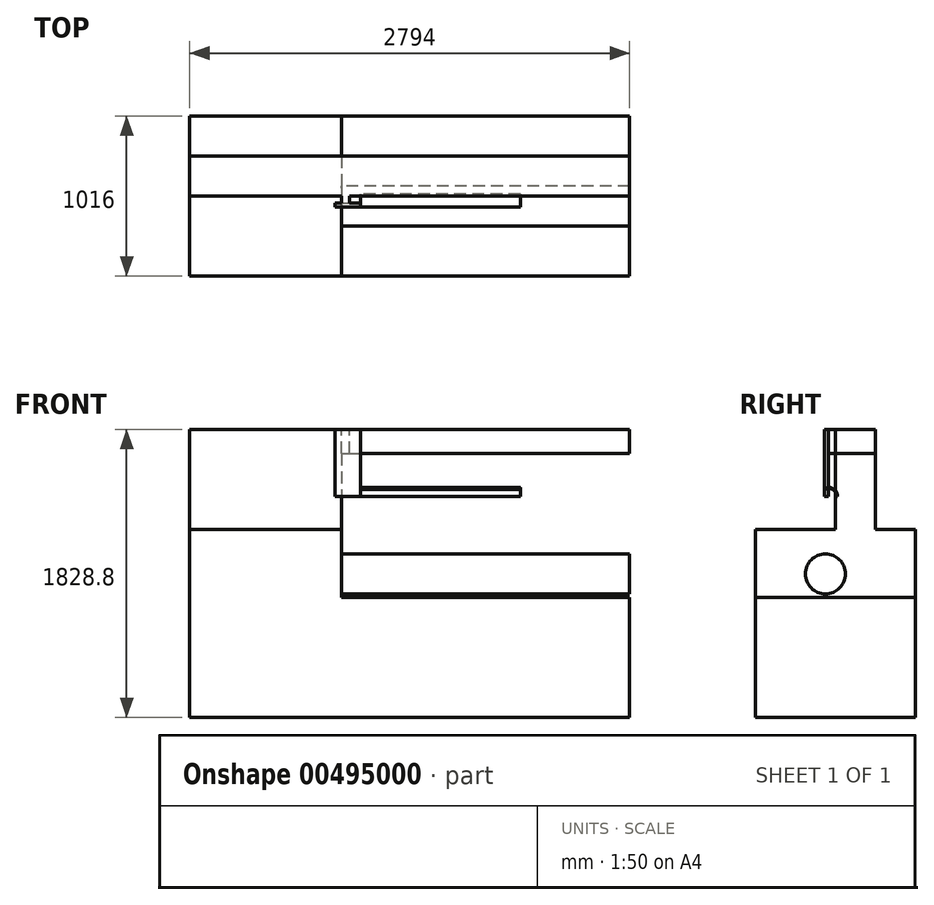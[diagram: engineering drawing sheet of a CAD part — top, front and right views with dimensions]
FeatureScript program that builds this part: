
annotation { "Feature Type Name" : "Feature", "Feature Type Description" : "" }
export const myFeature = defineFeature(function(context is Context, id is Id, definition is map)
    precondition{}
    {
        {
            var Q0;
            Q0=qCreatedBy(makeId("Front.planeOp"),FACE);
            var sketch = newSketch(context, id + "F0", { "sketchPlane" : qUnion([Q0])});
            skLineSegment(sketch, "E0.bottom", {"start": v(0, 0) * mm, "end": v(2794, 0) * mm});
            skLineSegment(sketch, "E0.top", {"start": v(0, 1828.8) * mm, "end": v(2794, 1828.8) * mm});
            skLineSegment(sketch, "E0.left", {"start": v(0, 0) * mm, "end": v(0, 1828.8) * mm});
            skLineSegment(sketch, "E0.right", {"start": v(2794, 0) * mm, "end": v(2794, 1828.8) * mm});
            skSolve(sketch);
        }
        {
            var Q0;
            Q0=makeQuery(id+"F0.imprint","IMPRINT",FACE,{"disambiguationData":[TD([[makeQuery(id+"F0.imprint","IMPRINT",EDGE,{"derivedFrom":sQuery(id+"F0.wireOp",EDGE,"E0.bottom")}),1.0]])]});
            extrude(context, id + "F1", {"entities" : qUnion([Q0]), "oppositeDirection" : true, "depth" : 1016 * mm});
        }
        {
            var Q0;
            Q0=makeQuery(id+"F1.opExtrude","CAP_FACE",FACE,{"disambiguationData":[OSD([sQuery(id+"F0.wireOp",EDGE,"E0.bottom"),sQuery(id+"F0.wireOp",EDGE,"E0.top"),sQuery(id+"F0.wireOp",EDGE,"E0.left"),sQuery(id+"F0.wireOp",EDGE,"E0.right")])],"isStart":true});
            var sketch = newSketch(context, id + "F2", { "sketchPlane" : qUnion([Q0])});
            skLineSegment(sketch, "E1.bottom", {"start": v(2794, 762) * mm, "end": v(965.2, 762) * mm});
            skLineSegment(sketch, "E1.top", {"start": v(2794, 1676.4) * mm, "end": v(965.2, 1676.4) * mm});
            skLineSegment(sketch, "E1.left", {"start": v(2794, 762) * mm, "end": v(2794, 1676.4) * mm});
            skLineSegment(sketch, "E1.right", {"start": v(965.2, 762) * mm, "end": v(965.2, 1676.4) * mm});
            skSolve(sketch);
        }
        {
            var Q0;
            Q0=makeQuery(id+"F2.imprint","IMPRINT",FACE,{"disambiguationData":[TD([[makeQuery(id+"F2.imprint","IMPRINT",EDGE,{"derivedFrom":sQuery(id+"F2.wireOp",EDGE,"E1.bottom")}),-1.0]])]});
            extrude(context, id + "F3", {"entities" : qUnion([Q0]), "operationType" : NewBodyOperationType.REMOVE, "endBound" : BoundingType.THROUGH_ALL, "oppositeDirection" : true, "depth" : 1016 * mm});
        }
        {
            var Q0;
            Q0=makeQuery(id+"F1.opExtrude","SWEPT_FACE",FACE,{"disambiguationData":[OSD([sQuery(id+"F0.wireOp",EDGE,"E0.top")])]});
            var sketch = newSketch(context, id + "F4", { "sketchPlane" : qUnion([Q0])});
            skLineSegment(sketch, "E2.bottom", {"start": v(0, 0) * mm, "end": v(2794, 0) * mm});
            skLineSegment(sketch, "E2.top", {"start": v(0, 508) * mm, "end": v(2794, 508) * mm});
            skLineSegment(sketch, "E2.left", {"start": v(0, 0) * mm, "end": v(0, 508) * mm});
            skLineSegment(sketch, "E2.right", {"start": v(2794, 0) * mm, "end": v(2794, 508) * mm});
            skSolve(sketch);
        }
        {
            var Q0;
            Q0=makeQuery(id+"F4.imprint","IMPRINT",FACE,{"disambiguationData":[TD([[makeQuery(id+"F4.imprint","IMPRINT",EDGE,{"derivedFrom":sQuery(id+"F4.wireOp",EDGE,"E2.bottom")}),1.0]])]});
            extrude(context, id + "F5", {"entities" : qUnion([Q0]), "operationType" : NewBodyOperationType.REMOVE, "oppositeDirection" : true, "depth" : 635 * mm});
        }
        {
            var Q0;
            Q0=makeQuery(id+"F1.opExtrude","SWEPT_FACE",FACE,{"disambiguationData":[OSD([sQuery(id+"F0.wireOp",EDGE,"E0.top")])]});
            var sketch = newSketch(context, id + "F6", { "sketchPlane" : qUnion([Q0])});
            skLineSegment(sketch, "E3.bottom", {"start": v(0, 1016) * mm, "end": v(2794, 1016) * mm});
            skLineSegment(sketch, "E3.top", {"start": v(0, 762) * mm, "end": v(2794, 762) * mm});
            skLineSegment(sketch, "E3.left", {"start": v(0, 1016) * mm, "end": v(0, 762) * mm});
            skLineSegment(sketch, "E3.right", {"start": v(2794, 1016) * mm, "end": v(2794, 762) * mm});
            skSolve(sketch);
        }
        {
            var Q0;
            Q0=makeQuery(id+"F6.imprint","IMPRINT",FACE,{"disambiguationData":[TD([[makeQuery(id+"F6.imprint","IMPRINT",EDGE,{"derivedFrom":sQuery(id+"F6.wireOp",EDGE,"E3.bottom")}),-1.0]])]});
            extrude(context, id + "F7", {"entities" : qUnion([Q0]), "operationType" : NewBodyOperationType.REMOVE, "oppositeDirection" : true, "depth" : 635 * mm});
        }
        {
            var Q0;
            Q0=makeQuery(id+"F3.boolean.opBoolean","COPY",FACE,{"derivedFrom":makeQuery(id+"F3.opExtrude","SWEPT_FACE",FACE,{"disambiguationData":[OSD([sQuery(id+"F2.wireOp",EDGE,"E1.right")])]})});
            var sketch = newSketch(context, id + "F8", { "sketchPlane" : qUnion([Q0])});
            skCircle(sketch, "E4", {"center": v(442.96, 911.98) * mm, "radius": 127 * mm});
            skSolve(sketch);
        }
        {
            var Q0;
            Q0 = qSketchRegion(id + "F8", true);
            extrude(context, id + "F9", {"entities" : qUnion([Q0]), "operationType" : NewBodyOperationType.ADD, "depth" : 1828.8 * mm});
        }
        {
            var Q0;
            Q0=makeQuery(id+"F5.boolean.opBoolean","COPY",FACE,{"derivedFrom":makeQuery(id+"F5.opExtrude","SWEPT_FACE",FACE,{"disambiguationData":[OSD([sQuery(id+"F4.wireOp",EDGE,"E2.top")])]})});
            var sketch = newSketch(context, id + "F10", { "sketchPlane" : qUnion([Q0])});
            skLineSegment(sketch, "E5.bottom", {"start": v(965.2, 1676.4) * mm, "end": v(1016, 1676.4) * mm});
            skLineSegment(sketch, "E5.top", {"start": v(965.2, 1828.8) * mm, "end": v(1016, 1828.8) * mm});
            skLineSegment(sketch, "E5.left", {"start": v(965.2, 1676.4) * mm, "end": v(965.2, 1828.8) * mm});
            skLineSegment(sketch, "E5.right", {"start": v(1016, 1676.4) * mm, "end": v(1016, 1828.8) * mm});
            skSolve(sketch);
        }
        {
            var Q0;
            Q0=makeQuery(id+"F10.imprint","IMPRINT",FACE,{"disambiguationData":[TD([[makeQuery(id+"F10.imprint","IMPRINT",EDGE,{"derivedFrom":sQuery(id+"F10.wireOp",EDGE,"E5.bottom")}),1.0]])]});
            extrude(context, id + "F11", {"entities" : qUnion([Q0]), "operationType" : NewBodyOperationType.ADD, "depth" : 44.45 * mm});
        }
        {
            var Q0;
            Q0=makeQuery(id+"F11.opExtrude","CAP_FACE",FACE,{"disambiguationData":[OSD([sQuery(id+"F10.wireOp",EDGE,"E5.bottom"),sQuery(id+"F10.wireOp",EDGE,"E5.top"),sQuery(id+"F10.wireOp",EDGE,"E5.left"),sQuery(id+"F10.wireOp",EDGE,"E5.right")])],"isStart":false});
            var sketch = newSketch(context, id + "F12", { "sketchPlane" : qUnion([Q0])});
            skLineSegment(sketch, "E6.bottom", {"start": v(1083.52, 1828.8) * mm, "end": v(922.15, 1828.8) * mm});
            skLineSegment(sketch, "E6.top", {"start": v(1083.52, 1403.65) * mm, "end": v(922.15, 1403.65) * mm});
            skLineSegment(sketch, "E6.left", {"start": v(1083.52, 1828.8) * mm, "end": v(1083.52, 1403.65) * mm});
            skLineSegment(sketch, "E6.right", {"start": v(922.15, 1828.8) * mm, "end": v(922.15, 1403.65) * mm});
            skSolve(sketch);
        }
        {
            var Q0;
            Q0 = qSketchRegion(id + "F12", true);
            extrude(context, id + "F13", {"entities" : qUnion([Q0]), "operationType" : NewBodyOperationType.ADD, "depth" : 25.4 * mm});
        }
        {
            var Q0;
            Q0=makeQuery(id+"F13.opExtrude","SWEPT_FACE",FACE,{"disambiguationData":[OSD([sQuery(id+"F12.wireOp",EDGE,"E6.left")])]});
            var sketch = newSketch(context, id + "F14", { "sketchPlane" : qUnion([Q0])});
            skArc(sketch, "E7", {"start": v(520.57, 1403.65) * mm, "mid": v(493.57, 1452.13) * mm, "end": v(438.15, 1454.7) * mm});
            skArc(sketch, "E8.0", {"start": v(514.22, 1403.65) * mm, "mid": v(490.23, 1446.73) * mm, "end": v(440.98, 1449.02) * mm});
            skLineSegment(sketch, "E9", {"start": v(440.98, 1449.02) * mm, "end": v(438.15, 1454.7) * mm});
            skLineSegment(sketch, "E10", {"start": v(514.22, 1403.65) * mm, "end": v(520.57, 1403.65) * mm});
            skSolve(sketch);
        }
        {
            var Q0;
            {var subQ0=sQuery(id+"F14.wireOp",EDGE,"E10");Q0=makeQuery(id+"F14.imprint","IMPRINT",FACE,{"disambiguationData":[TD([[makeQuery(id+"F14.imprint","IMPRINT",EDGE,{"derivedFrom":subQ0}),1.0]])]});}
            var Q1;
            {var subQ0=sQuery(id+"F14.wireOp",EDGE,"E9");Q1=makeQuery(id+"F14.imprint","IMPRINT",FACE,{"disambiguationData":[TD([[makeQuery(id+"F14.imprint","IMPRINT",EDGE,{"derivedFrom":subQ0}),-1.0]])]});}
            extrude(context, id + "F15", {"entities" : qUnion([Q0, Q1]), "operationType" : NewBodyOperationType.ADD, "depth" : 1016 * mm});
        }
    });
